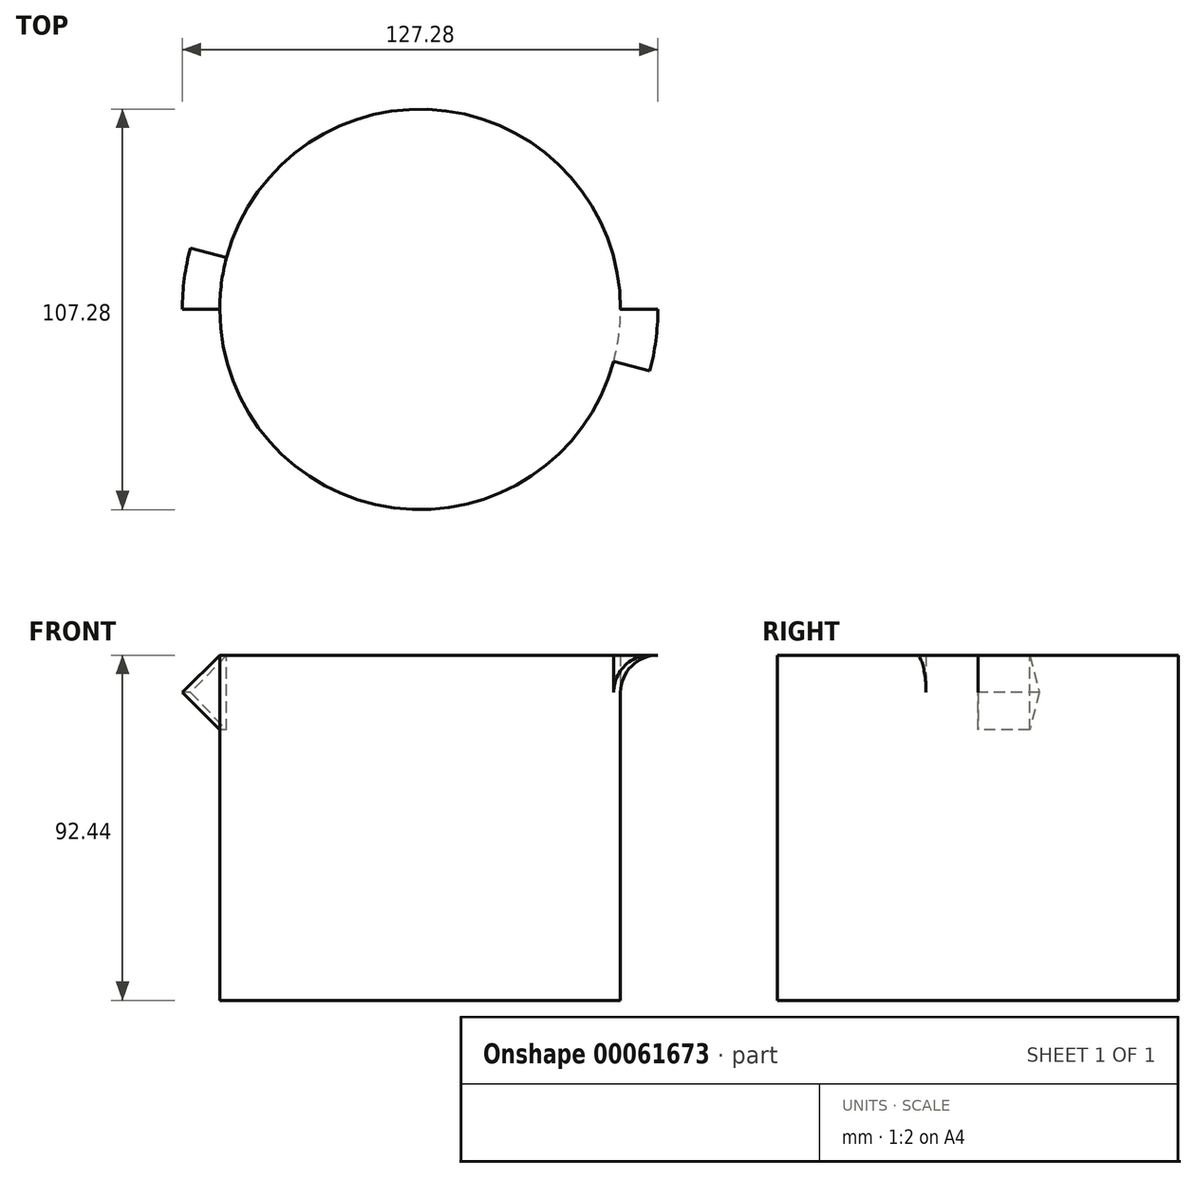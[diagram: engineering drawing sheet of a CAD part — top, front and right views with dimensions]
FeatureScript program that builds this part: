
annotation { "Feature Type Name" : "Feature", "Feature Type Description" : "" }
export const myFeature = defineFeature(function(context is Context, id is Id, definition is map)
    precondition{}
    {
        {
            var Q0;
            Q0=qCreatedBy(makeId("Top.planeOp"),FACE);
            var sketch = newSketch(context, id + "F0", { "sketchPlane" : qUnion([Q0])});
            skCircle(sketch, "E0", {"center": v(0, 0) * mm, "radius": 53.64 * mm});
            skSolve(sketch);
        }
        {
            var Q0;
            Q0 = qSketchRegion(id + "F0", true);
            var Q1;
            Q1=makeQuery(id+"F0.imprint","IMPRINT",FACE,{"disambiguationData":[TD([[makeQuery(id+"F0.imprint","IMPRINT",EDGE,{"derivedFrom":sQuery(id+"F0.wireOp",EDGE,"E0")}),1.0]])]});
            extrude(context, id + "F1", {"entities" : qUnion([Q0, Q1]), "depth" : 92.44 * mm});
        }
        {
            var Q0;
            Q0=qCreatedBy(makeId("Front.planeOp"),FACE);
            var sketch = newSketch(context, id + "F2", { "sketchPlane" : qUnion([Q0])});
            skLineSegment(sketch, "E1", {"start": v(-53.64, 0) * mm, "end": v(-53.64, 92.44) * mm});
            skLineSegment(sketch, "E2", {"start": v(53.64, 92.44) * mm, "end": v(53.64, 0) * mm});
            skLineSegment(sketch, "E3", {"start": v(53.64, 92.44) * mm, "end": v(63.64, 92.44) * mm});
            skArc(sketch, "E4", {"start": v(63.64, 92.44) * mm, "mid": v(56.57, 89.52) * mm, "end": v(53.64, 82.44) * mm});
            skLineSegment(sketch, "E5", {"start": v(-53.64, 92.44) * mm, "end": v(-63.64, 82.44) * mm});
            skLineSegment(sketch, "E6", {"start": v(-63.64, 82.44) * mm, "end": v(-53.64, 72.44) * mm});
            skSolve(sketch);
        }
        {
            var Q0;
            {var subQ0=sQuery(id+"F2.wireOp",EDGE,"E3");Q0=makeQuery(id+"F2.imprint","IMPRINT",FACE,{"disambiguationData":[TD([[makeQuery(id+"F2.imprint","IMPRINT",EDGE,{"derivedFrom":subQ0}),-1.0]])]});}
            var Q1;
            Q1=makeQuery(id+"F1.opExtrude","SWEPT_FACE",FACE,{"disambiguationData":[OSD([sQuery(id+"F0.wireOp",EDGE,"E0")])]});
            revolve(context, id + "F3", {"operationType" : NewBodyOperationType.ADD, "entities" : qUnion([Q0]), "axis" : qUnion([Q1]), "revolveType" : RevolveType.ONE_DIRECTION, "angle" : 15 * degree});
        }
        {
            var Q0;
            {var subQ0=sQuery(id+"F2.wireOp",EDGE,"E5");Q0=makeQuery(id+"F2.imprint","IMPRINT",FACE,{"disambiguationData":[TD([[makeQuery(id+"F2.imprint","IMPRINT",EDGE,{"derivedFrom":subQ0}),1.0]])]});}
            var Q1;
            Q1=makeQuery(id+"F1.opExtrude","SWEPT_FACE",FACE,{"disambiguationData":[OSD([sQuery(id+"F0.wireOp",EDGE,"E0")])]});
            revolve(context, id + "F4", {"operationType" : NewBodyOperationType.ADD, "entities" : qUnion([Q0]), "axis" : qUnion([Q1]), "revolveType" : RevolveType.ONE_DIRECTION, "angle" : 15 * degree});
        }
    });
